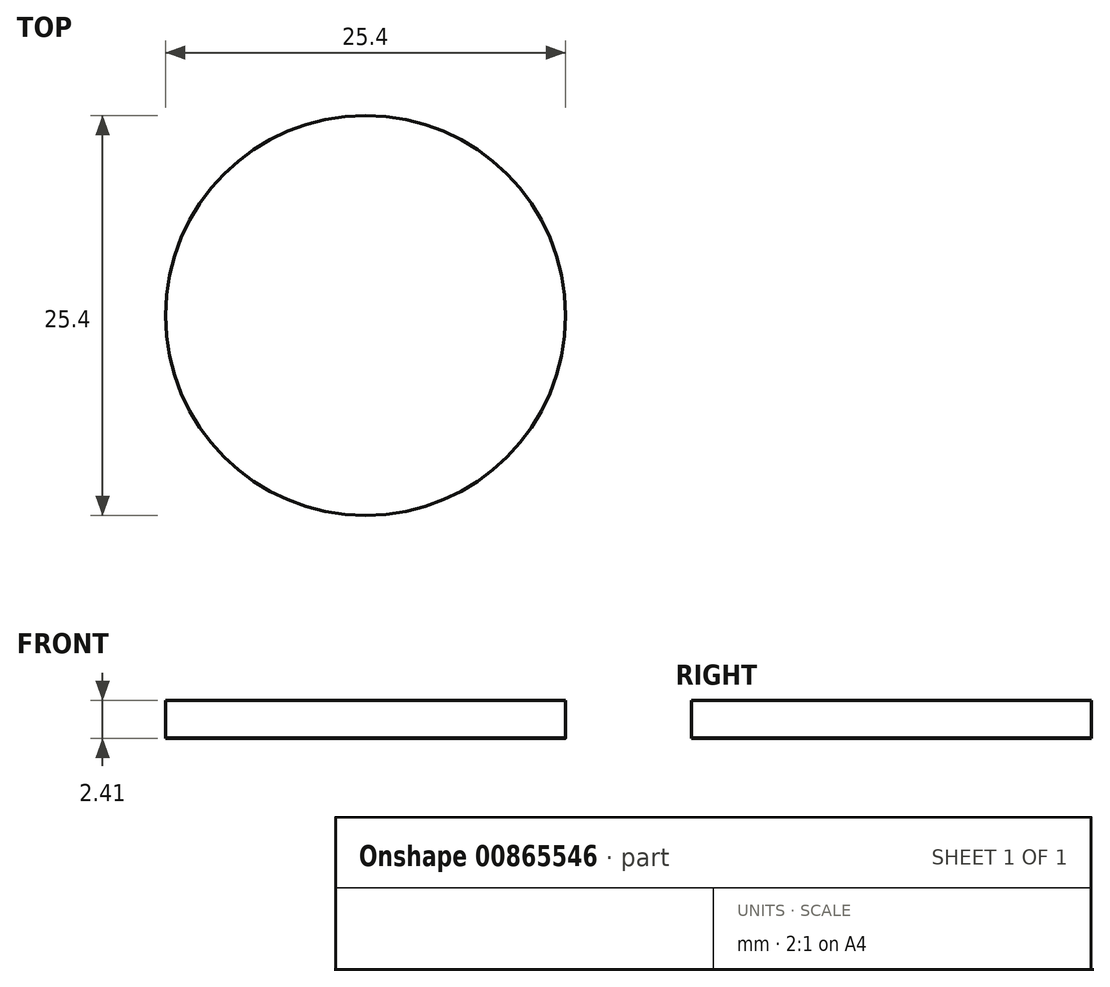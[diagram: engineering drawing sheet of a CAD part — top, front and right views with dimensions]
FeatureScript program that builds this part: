
annotation { "Feature Type Name" : "Feature", "Feature Type Description" : "" }
export const myFeature = defineFeature(function(context is Context, id is Id, definition is map)
    precondition{}
    {
        {
            var Q0;
            Q0=qCreatedBy(makeId("Top.planeOp"),FACE);
            var sketch = newSketch(context, id + "F0", { "sketchPlane" : qUnion([Q0])});
            skCircle(sketch, "E0", {"center": v(0, 0) * mm, "radius": 12.7 * mm});
            skSolve(sketch);
        }
        {
            var Q0;
            Q0=makeQuery(id+"F0.imprint","IMPRINT",FACE,{"disambiguationData":[TD([[makeQuery(id+"F0.imprint","IMPRINT",EDGE,{"derivedFrom":sQuery(id+"F0.wireOp",EDGE,"E0")}),1.0]])]});
            extrude(context, id + "F1", {"entities" : qUnion([Q0]), "depth" : 1.25 / 50.8 * mm, "offsetDistance" : 25.4 * mm});
        }
        {
            var Q0;
            Q0=makeQuery(id+"F1.opExtrude","CAP_FACE",FACE,{"disambiguationData":[OSD([sQuery(id+"F0.wireOp",EDGE,"E0")])],"isStart":false});
            var sketch = newSketch(context, id + "F2", { "sketchPlane" : qUnion([Q0])});
            skCircle(sketch, "E1", {"center": v(0, 0) * mm, "radius": 12.7 * mm});
            skSolve(sketch);
        }
        {
            var Q0;
            Q0=qSketchRegion(id+"F2",true);
            extrude(context, id + "F3", {"entities" : qUnion([Q0]), "depth" : 2.38 * mm, "offsetDistance" : 25.4 * mm});
        }
    });
